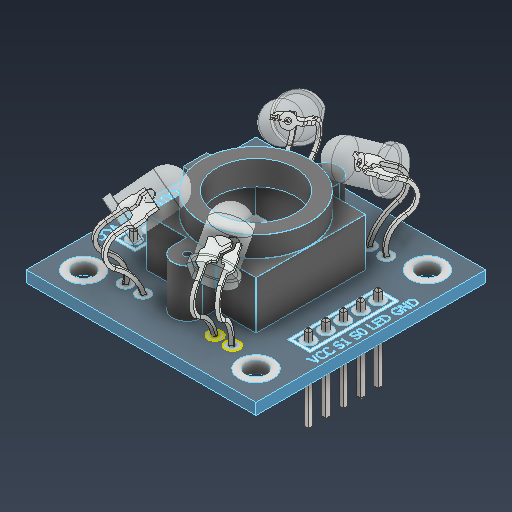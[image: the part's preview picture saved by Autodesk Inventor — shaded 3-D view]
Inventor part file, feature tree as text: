
AUTODESK INVENTOR PART (.ipt)
format: ipt  version: 2021 (Build 250183000, 183)  size: 2,315,776 bytes
history: native  units: mm
features: other x25, sketch x4
ambient origin geometry x8: Origin, YZ Plane, XZ Plane, XY Plane, X Axis, Y Axis, Z Axis, Center Point
bodies: Solid1 (feature_tree), Solid2 (feature_tree), Solid3 (feature_tree), Solid4 (feature_tree), Solid5 (feature_tree), Solid6 (feature_tree), Solid7 (feature_tree), Solid8 (feature_tree), Solid9 (feature_tree), Solid10 (feature_tree), Solid11 (feature_tree), Solid12 (feature_tree), Solid13 (feature_tree), Solid14 (feature_tree), Solid15 (feature_tree), Solid16 (feature_tree), Solid17 (feature_tree), Solid18 (feature_tree), Solid19 (feature_tree), Solid20 (feature_tree), Solid21 (feature_tree), Solid22 (feature_tree)
feature tree (29):
  other  "Repaired Geometry1"
  sketch  "3D Sketch1"
  sketch  "Sketch19"
  sketch  "Sketch20"
  sketch  "3D Sketch4"
  other  "Color_sensor_PCB_1:1"
  other  "Pin Header 1x5 TH Pitch 2.54mm_1:1"
  other  "Pin Header 1x5 TH Pitch 2.54mm_1:2"
  other  "Pin Header 1x5 TH Pitch 2.54mm_1:3"
  other  "Pin Header 1x5 TH Pitch 2.54mm_1:4"
  other  "Pin Header 1x5 TH Pitch 2.54mm_1:5"
  other  "Pin Header 1x5 TH Pitch 2.54mm_1:6"
  other  "Pin Header 1x5 TH Pitch 2.54mm_2:1"
  other  "Pin Header 1x5 TH Pitch 2.54mm_2:2"
  other  "Pin Header 1x5 TH Pitch 2.54mm_2:3"
  other  "Pin Header 1x5 TH Pitch 2.54mm_2:4"
  other  "Pin Header 1x5 TH Pitch 2.54mm_2:5"
  other  "Pin Header 1x5 TH Pitch 2.54mm_2:6"
  other  "TCS3200_1:1"
  other  "5mm LED_1:1"
  other  "5mm LED_1:2"
  other  "5mm LED_MIR_1:1"
  other  "5mm LED_MIR_1:2"
  other  "5mm LED_MIR1_1:1"
  other  "5mm LED_MIR1_1:2"
  other  "5mm LED_MIR_MIR_1:1"
  other  "5mm LED_MIR_MIR_1:2"
  other  "Composite1"
  other  "Srf1"
